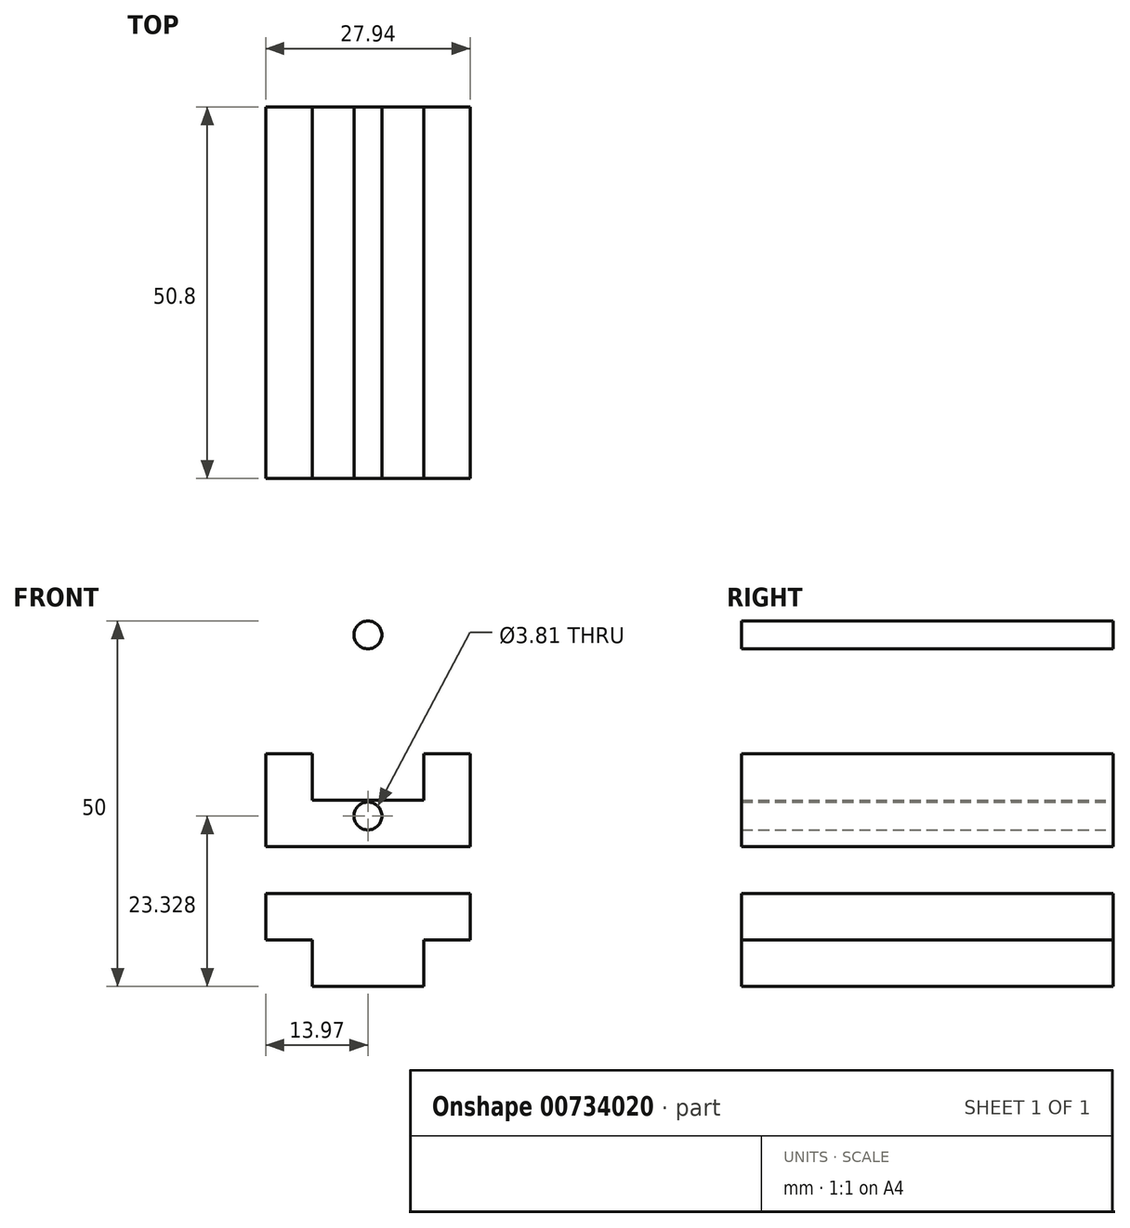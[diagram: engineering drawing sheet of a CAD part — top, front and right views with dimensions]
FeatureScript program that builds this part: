
annotation { "Feature Type Name" : "Feature", "Feature Type Description" : "" }
export const myFeature = defineFeature(function(context is Context, id is Id, definition is map)
    precondition{}
    {
        {
            var Q0;
            Q0=qCreatedBy(makeId("Front.planeOp"),FACE);
            var sketch = newSketch(context, id + "F0", { "sketchPlane" : qUnion([Q0])});
            skLineSegment(sketch, "E0", {"start": v(0, 0) * mm, "end": v(7.62, 0) * mm});
            skLineSegment(sketch, "E1", {"start": v(7.62, 0) * mm, "end": v(7.62, 6.35) * mm});
            skLineSegment(sketch, "E2", {"start": v(7.62, 6.35) * mm, "end": v(13.97, 6.35) * mm});
            skLineSegment(sketch, "E3", {"start": v(13.97, 6.35) * mm, "end": v(13.97, -6.35) * mm});
            skLineSegment(sketch, "E4", {"start": v(0, 0) * mm, "end": v(-7.62, 0) * mm});
            skLineSegment(sketch, "E5", {"start": v(-7.62, 0) * mm, "end": v(-7.62, 6.35) * mm});
            skLineSegment(sketch, "E6", {"start": v(-7.62, 6.35) * mm, "end": v(-13.97, 6.35) * mm});
            skLineSegment(sketch, "E7", {"start": v(-13.97, 6.35) * mm, "end": v(-13.97, -6.35) * mm});
            skLineSegment(sketch, "E8", {"start": v(-13.97, -6.35) * mm, "end": v(13.97, -6.35) * mm});
            skLineSegment(sketch, "E9", {"start": v(0, -6.35) * mm, "end": v(0, -12.81) * mm});
            skLineSegment(sketch, "E10", {"start": v(0, -12.81) * mm, "end": v(13.97, -12.81) * mm});
            skLineSegment(sketch, "E11", {"start": v(0, -12.81) * mm, "end": v(-13.97, -12.81) * mm});
            skLineSegment(sketch, "E12", {"start": v(-13.97, -12.81) * mm, "end": v(-13.97, -19.16) * mm});
            skLineSegment(sketch, "E13", {"start": v(-13.97, -19.16) * mm, "end": v(-7.62, -19.16) * mm});
            skLineSegment(sketch, "E14", {"start": v(-7.62, -19.16) * mm, "end": v(-7.62, -25.51) * mm});
            skLineSegment(sketch, "E15", {"start": v(-7.62, -25.51) * mm, "end": v(7.62, -25.51) * mm});
            skLineSegment(sketch, "E16", {"start": v(7.62, -25.51) * mm, "end": v(7.62, -19.16) * mm});
            skLineSegment(sketch, "E17", {"start": v(7.62, -19.16) * mm, "end": v(13.97, -19.16) * mm});
            skLineSegment(sketch, "E18", {"start": v(13.97, -12.81) * mm, "end": v(13.97, -19.16) * mm});
            skCircle(sketch, "E19", {"center": v(0, 22.58) * mm, "radius": 1.9 * mm});
            skSolve(sketch);
        }
        {
            var Q0;
            Q0=makeQuery(id+"F0.imprint","IMPRINT",FACE,{"disambiguationData":[TD([[makeQuery(id+"F0.imprint","IMPRINT",EDGE,{"derivedFrom":sQuery(id+"F0.wireOp",EDGE,"E0")}),-1.0]])]});
            extrude(context, id + "F1", {"entities" : qUnion([Q0]), "depth" : 50.8 * mm, "offsetDistance" : 25.4 * mm});
        }
        {
            var Q0;
            Q0=makeQuery(id+"F1.opExtrude","CAP_FACE",FACE,{"disambiguationData":[OSD([sQuery(id+"F0.wireOp",EDGE,"E0"),sQuery(id+"F0.wireOp",EDGE,"E1"),sQuery(id+"F0.wireOp",EDGE,"E2"),sQuery(id+"F0.wireOp",EDGE,"E3"),sQuery(id+"F0.wireOp",EDGE,"E4"),sQuery(id+"F0.wireOp",EDGE,"E5"),sQuery(id+"F0.wireOp",EDGE,"E6"),sQuery(id+"F0.wireOp",EDGE,"E7"),sQuery(id+"F0.wireOp",EDGE,"E8")])],"isStart":false});
            var sketch = newSketch(context, id + "F2", { "sketchPlane" : qUnion([Q0])});
            skCircle(sketch, "E20", {"center": v(0, -3.18) * mm, "radius": 1.9 * mm});
            skSolve(sketch);
        }
        {
            var Q0;
            Q0 = qSketchRegion(id + "F2", true);
            extrude(context, id + "F3", {"entities" : qUnion([Q0]), "operationType" : NewBodyOperationType.REMOVE, "oppositeDirection" : true, "depth" : 50.8 * mm, "offsetDistance" : 25.4 * mm});
        }
        {
            var Q0;
            Q0 = qSketchRegion(id + "F0", true);
            extrude(context, id + "F4", {"entities" : qUnion([Q0]), "operationType" : NewBodyOperationType.ADD, "depth" : 50.8 * mm, "offsetDistance" : 25.4 * mm});
        }
        {
            var Q0;
            Q0=makeQuery(id+"F0.imprint","IMPRINT",FACE,{"disambiguationData":[TD([[makeQuery(id+"F0.imprint","IMPRINT",EDGE,{"derivedFrom":sQuery(id+"F0.wireOp",EDGE,"E19")}),1.0]])]});
            extrude(context, id + "F5", {"entities" : qUnion([Q0]), "operationType" : NewBodyOperationType.ADD, "depth" : 50.8 * mm, "offsetDistance" : 25.4 * mm});
        }
        {
            var Q0;
            {var subQ0=sQuery(id+"F0.wireOp",EDGE,"E8");var subQ1=sQuery(id+"F0.wireOp",EDGE,"E7");var subQ2=sQuery(id+"F0.wireOp",EDGE,"E6");var subQ3=sQuery(id+"F0.wireOp",EDGE,"E5");var subQ4=sQuery(id+"F0.wireOp",EDGE,"E4");var subQ5=sQuery(id+"F0.wireOp",EDGE,"E3");var subQ6=sQuery(id+"F0.wireOp",EDGE,"E2");var subQ7=sQuery(id+"F0.wireOp",EDGE,"E1");var subQ8=sQuery(id+"F0.wireOp",EDGE,"E0");Q0=makeQuery(id+"F4.boolean.opBoolean","MERGE",FACE,{"derivedFrom":[makeQuery(id+"F1.opExtrude","CAP_FACE",FACE,{"disambiguationData":[OSD([subQ8,subQ7,subQ6,subQ5,subQ4,subQ3,subQ2,subQ1,subQ0])],"isStart":true}),makeQuery(id+"F4.opExtrude","CAP_FACE",FACE,{"disambiguationData":[OSD([subQ8,subQ7,subQ6,subQ5,subQ4,subQ3,subQ2,subQ1,subQ0])],"isStart":true})]});}
            var sketch = newSketch(context, id + "F6", { "sketchPlane" : qUnion([Q0])});
            skCircle(sketch, "E21", {"center": v(0, -2.18) * mm, "radius": 1.9 * mm});
            skSolve(sketch);
        }
        {
            var Q0;
            Q0 = qSketchRegion(id + "F6", true);
            extrude(context, id + "F7", {"entities" : qUnion([Q0]), "operationType" : NewBodyOperationType.REMOVE, "oppositeDirection" : true, "depth" : 50.8 * mm, "offsetDistance" : 25.4 * mm});
        }
    });
